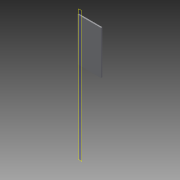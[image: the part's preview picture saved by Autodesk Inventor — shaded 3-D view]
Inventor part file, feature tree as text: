
AUTODESK INVENTOR PART (.ipt)
format: ipt  version: 2015 (Build 190159000, 159)  size: 141,824 bytes
history: native  units: in
note: dims shown in document units (in); Inventor stores cm internally (conversion verified against a paired STEP export)
features: reference x9, extrude x2, sketch x2, plane x1
ambient origin geometry x8: Origin, YZ Plane, XZ Plane, XY Plane, X Axis, Y Axis, Z Axis, Center Point
bodies: Solid1 (feature_tree)
feature tree (14):
  plane  "Work Plane1"
  extrude  "Extrusion1"  Depth=0.25in TaperAngle=0.0deg
  extrude  "Extrusion2"  [1 undecoded]
  sketch  "Sketch1"  dims[d0=0.25in d1=0.0in d2=0.25in d3=0.0in]
  reference  "Reference1"
  reference  "Reference2"
  reference  "Reference3"
  reference  "Reference4"
  reference  "Reference5"
  sketch  "Sketch2"
  reference  "Reference6"
  reference  "Reference7"
  reference  "Reference8"
  reference  "Reference9"
note: 1 required parameter value undecoded (feature->parameter linkage not recoverable at this tier; creation-order binding heuristic only, values carry confidence <= 0.55)
